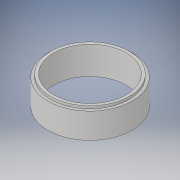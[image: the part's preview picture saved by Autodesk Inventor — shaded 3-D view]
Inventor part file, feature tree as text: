
AUTODESK INVENTOR PART (.ipt)
format: ipt  version: 2017 (Build 210142000, 142)  size: 138,240 bytes
history: native  units: in
note: dims shown in document units (in); Inventor stores cm internally (conversion verified against a paired STEP export)
features: revolve x1, sketch x1
ambient origin geometry x8: Origin, YZ Plane, XZ Plane, XY Plane, X Axis, Y Axis, Z Axis, Center Point
bodies: Body1 (feature_tree)
feature tree (2):
  revolve  "Revolution4"  [1 undecoded]
  sketch  "Sketch1"  dims[d0=1.13in d1=3.75in d2=0.25in d3=0.1718in d5=1.0in d6=1.0in d7=90.0deg d8=0.5in d9=15.0deg d11=0.25in d12=1.25in d13=0.25in d15=0.25in d16=0.5in d17=0.5in d18=0.5in d19=2.5in d20=0.5in d22=0.375in d23=0.25in d25=0.234in d26=15.0deg d30=90.0deg]
note: 1 required parameter value undecoded (feature->parameter linkage not recoverable at this tier; creation-order binding heuristic only, values carry confidence <= 0.55)
